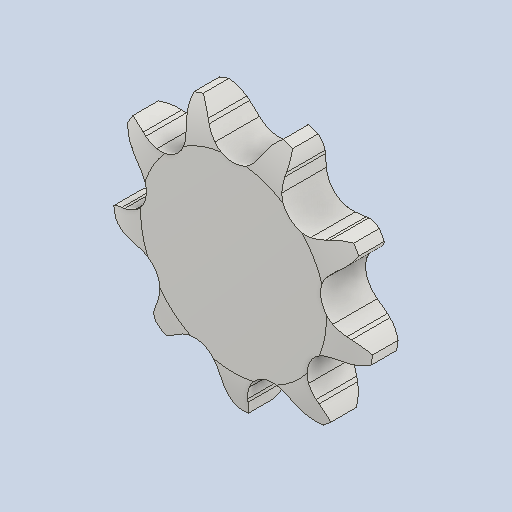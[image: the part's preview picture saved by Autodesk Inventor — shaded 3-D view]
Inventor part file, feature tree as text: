
AUTODESK INVENTOR PART (.ipt)
format: ipt  version: 2022.1 (Build 261234000, 234)  size: 375,296 bytes
history: native  units: mm
features: other x6, extrude x2, pattern_linear x1, pattern_circular x1
ambient origin geometry x8: Origin, YZ Plane, XZ Plane, XY Plane, X Axis, Y Axis, Z Axis, Center Point
bodies: Solid1 (feature_tree)
feature tree (10):
  other  "Perfil de diente teórico"
  other  "Perfil de diente"
  other  "Perfil de sección"
  other  "Cubierta"
  other  "Ramal"
  pattern_linear  "Patrón de ramal"  Spacing1=46.415395mm  [1 undecoded]
  extrude  "Diente teórico"  Depth=6.981317mm
  extrude  "Diente"  Depth=5.1308mm
  pattern_circular  "Patrón de diente"  [2 undecoded]
  other  "Plano síncrono"
note: 3 required parameter values undecoded (feature->parameter linkage not recoverable at this tier; creation-order binding heuristic only, values carry confidence <= 0.55)
